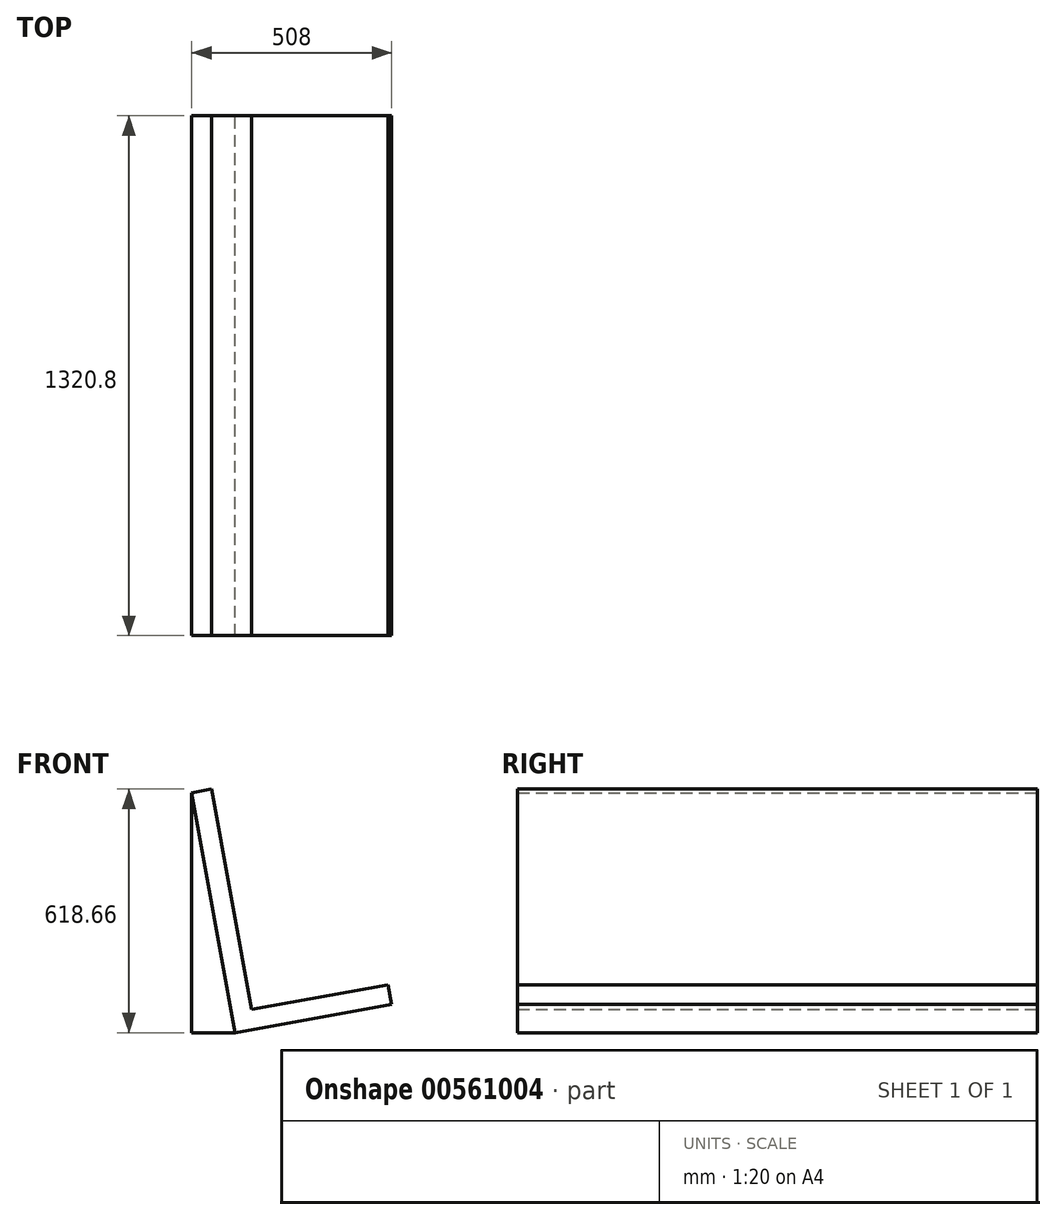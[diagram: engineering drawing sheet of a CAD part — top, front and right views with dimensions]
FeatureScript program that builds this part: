
annotation { "Feature Type Name" : "Feature", "Feature Type Description" : "" }
export const myFeature = defineFeature(function(context is Context, id is Id, definition is map)
    precondition{}
    {
        {
            var Q0;
            Q0=qCreatedBy(makeId("Front.planeOp"),FACE);
            var sketch = newSketch(context, id + "F0", { "sketchPlane" : qUnion([Q0])});
            skLineSegment(sketch, "E0", {"start": v(-55.28, 304.8) * mm, "end": v(55.28, -304.8) * mm});
            skLineSegment(sketch, "E1", {"start": v(55.28, -304.8) * mm, "end": v(452.72, -232.72) * mm});
            skLineSegment(sketch, "E2", {"start": v(-55.28, 304.8) * mm, "end": v(-55.28, -232.72) * mm, "construction": true});
            skLineSegment(sketch, "E3", {"start": v(-55.28, -232.72) * mm, "end": v(452.72, -232.72) * mm, "construction": true});
            skLineSegment(sketch, "E4", {"start": v(-55.28, 304.8) * mm, "end": v(-5.3, 313.86) * mm});
            skLineSegment(sketch, "E5", {"start": v(-5.3, 313.86) * mm, "end": v(96.2, -245.75) * mm});
            skLineSegment(sketch, "E6", {"start": v(96.2, -245.75) * mm, "end": v(443.66, -182.74) * mm});
            skLineSegment(sketch, "E7", {"start": v(443.66, -182.74) * mm, "end": v(452.72, -232.72) * mm});
            skLineSegment(sketch, "E8", {"start": v(-55.28, 304.8) * mm, "end": v(-55.28, -304.8) * mm});
            skLineSegment(sketch, "E9", {"start": v(-55.28, -304.8) * mm, "end": v(55.28, -304.8) * mm});
            skLineSegment(sketch, "E10", {"start": v(55.28, -304.8) * mm, "end": v(452.72, -304.8) * mm, "construction": true});
            skLineSegment(sketch, "E11", {"start": v(452.72, -304.8) * mm, "end": v(452.72, -232.72) * mm, "construction": true});
            skSolve(sketch);
        }
        {
            var Q0;
            Q0=makeQuery(id+"F0.imprint","IMPRINT",FACE,{"disambiguationData":[TD([[makeQuery(id+"F0.imprint","IMPRINT",EDGE,{"derivedFrom":sQuery(id+"F0.wireOp",EDGE,"E0")}),1.0]])]});
            extrude(context, id + "F1", {"entities" : qUnion([Q0]), "depth" : 1320.8 * mm, "offsetDistance" : 25.4 * mm});
        }
        {
            var Q0;
            Q0=makeQuery(id+"F0.imprint","IMPRINT",FACE,{"disambiguationData":[TD([[makeQuery(id+"F0.imprint","IMPRINT",EDGE,{"derivedFrom":sQuery(id+"F0.wireOp",EDGE,"E0")}),-1.0]])]});
            extrude(context, id + "F2", {"entities" : qUnion([Q0]), "depth" : 1320.8 * mm, "offsetDistance" : 25.4 * mm});
        }
    });
